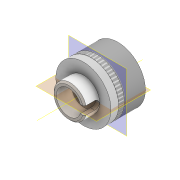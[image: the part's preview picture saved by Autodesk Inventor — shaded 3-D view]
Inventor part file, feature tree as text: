
AUTODESK INVENTOR PART (.ipt)
format: ipt  version: 2022 (Build 260153000, 153)  size: 766,464 bytes
history: native  units: mm
features: other x6, sketch x5, extrude x4, plane x2, revolve x1, projected_geometry x1
ambient origin geometry x8: Origin, YZ Plane, XZ Plane, XY Plane, X Axis, Y Axis, Z Axis, Center Point
bodies: Volumenkörper1 (feature_tree), Volumenkörper2 (feature_tree)
feature tree (19):
  other  "00_SM05FC2-Step.ipt"
  plane  "Arbeitsebene1"
  extrude  "Extrusion1"  [1 undecoded]
  plane  "Arbeitsebene2"
  revolve  "Umdrehung1"
  extrude  "Extrusion2"  TaperAngle=90.0deg  [1 undecoded]
  extrude  "Extrusion3"  Depth=12.12mm TaperAngle=0.0deg
  extrude  "Extrusion4"  TaperAngle=0.0deg  [1 undecoded]
  other  "Volumenkörper1::00_SM05FC2-Step.ipt"
  other  "Volumenkörper2::00_SM05FC2-Step.ipt"
  other  "Bezeichnung1"
  sketch  "Skizze1"  dims[d0=10.0mm d1=-0.5mm]
  other  "Arbeitsachse1"
  other  "Arbeitspunkt1"
  sketch  "Skizze2"  dims[d2=5.0mm d3=0.0mm d4=90.0deg]
  sketch  "Skizze3"  dims[d5=12.12mm d6=0.0mm d7=3.0mm d8=0.3mm d9=0.0mm d10=0.0mm]
  sketch  "Skizze4"  dims[d11=3.0mm d12=0.0mm d13=0.0mm]
  sketch  "Skizze5"
  projected_geometry  "Projizierte Kontur1"
note: 3 required parameter values undecoded (feature->parameter linkage not recoverable at this tier; creation-order binding heuristic only, values carry confidence <= 0.55)
